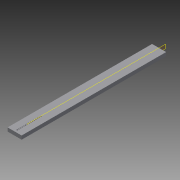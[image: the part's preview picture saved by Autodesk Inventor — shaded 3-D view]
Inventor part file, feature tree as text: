
AUTODESK INVENTOR PART (.ipt)
format: ipt  version: 2014 SP2 (Build 180246200, 246)  size: 92,160 bytes
history: native  units: in
note: dims shown in document units (in); Inventor stores cm internally (conversion verified against a paired STEP export)
features: extrude x2, sketch x2, plane x1, pattern_linear x1
ambient origin geometry x8: Origin, YZ Plane, XZ Plane, XY Plane, X Axis, Y Axis, Z Axis, Center Point
bodies: Solid1 (feature_tree)
feature tree (6):
  extrude  "Extrusion1"  Depth=0.45in
  plane  "Work Plane1"
  extrude  "Extrusion2"  Depth=18.0in
  pattern_linear  "Rectangular Pattern1"  Spacing1=1.0in  [1 undecoded]
  sketch  "Sketch1"  dims[d0=1.75in d1=0.45in]
  sketch  "Sketch2"  dims[d2=18.0in d3=0.0in d4=0.146in d5=1.0in d6=0.0in d7=5.9055in d9=0.21in]
note: 1 required parameter value undecoded (feature->parameter linkage not recoverable at this tier; creation-order binding heuristic only, values carry confidence <= 0.55)
